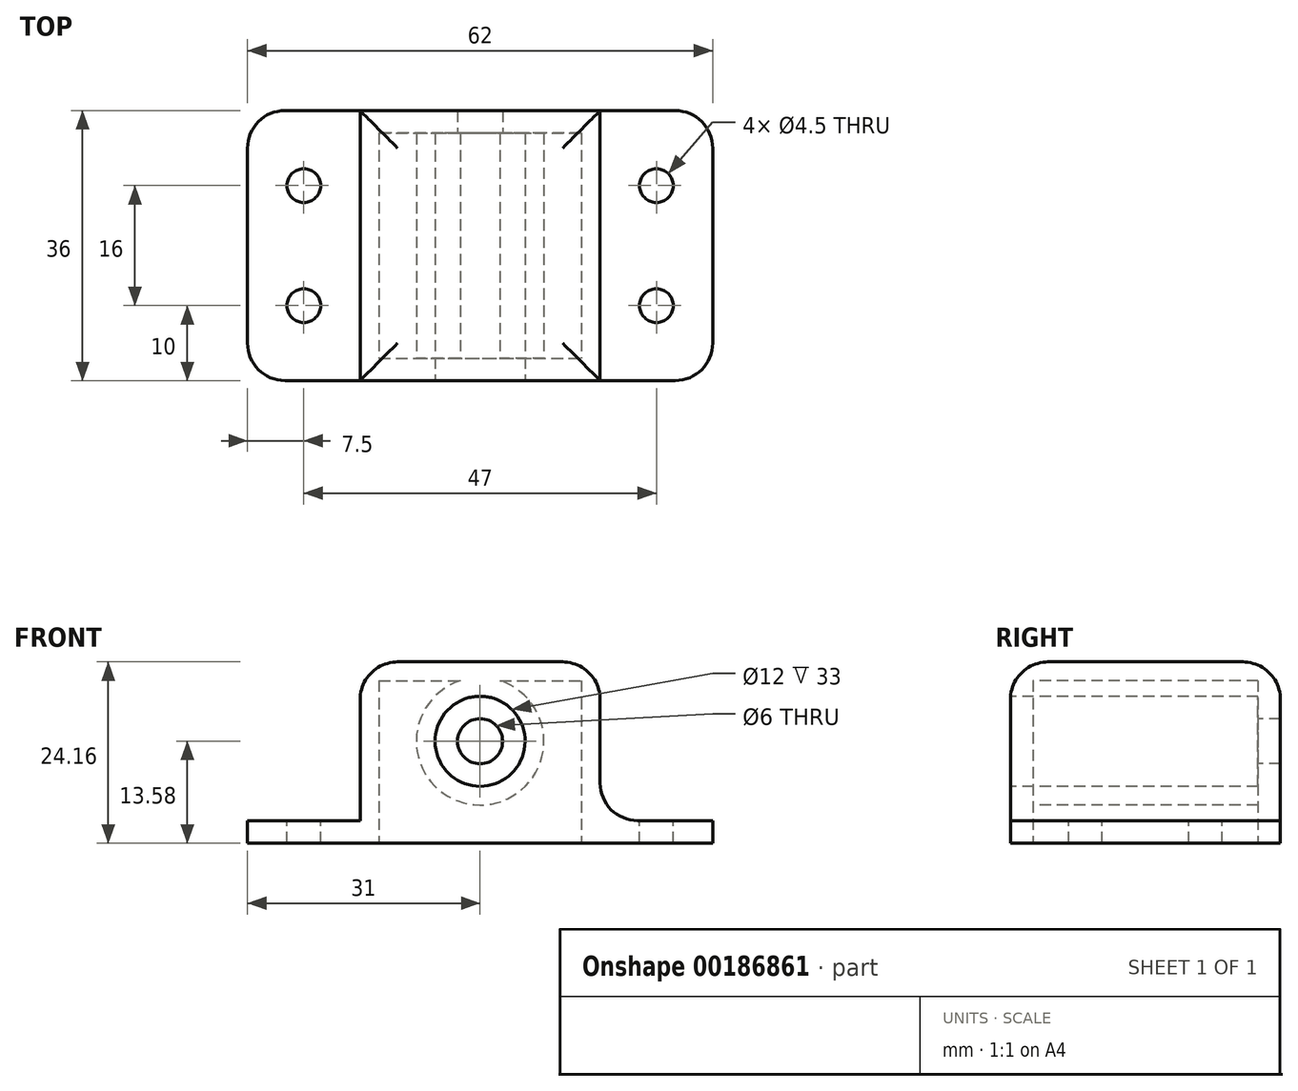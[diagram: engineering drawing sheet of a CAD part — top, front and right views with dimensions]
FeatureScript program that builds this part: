
annotation { "Feature Type Name" : "Feature", "Feature Type Description" : "" }
export const myFeature = defineFeature(function(context is Context, id is Id, definition is map)
    precondition{}
    {
        {
            var Q0;
            Q0=qCreatedBy(makeId("Front.planeOp"),FACE);
            var sketch = newSketch(context, id + "F0", { "sketchPlane" : qUnion([Q0])});
            skPoint(sketch, "E0", {"position": v(0, 0) * mm});
            skCircle(sketch, "E1.MirrorC", {"center": v(0, 0) * mm, "radius": 6 * mm});
            skLineSegment(sketch, "E2.bottom", {"start": v(-16, 10.58) * mm, "end": v(16, 10.58) * mm});
            skLineSegment(sketch, "E2.top", {"start": v(-16, -10.58) * mm, "end": v(16, -10.58) * mm});
            skLineSegment(sketch, "E2.left", {"start": v(-16, 10.58) * mm, "end": v(-16, -10.58) * mm});
            skLineSegment(sketch, "E2.right", {"start": v(16, 10.58) * mm, "end": v(16, -10.58) * mm});
            skSolve(sketch);
        }
        {
            var Q0;
            Q0=qSketchRegion(id+"F0",true);
            var Q1;
            Q1=makeQuery(id+"F0.imprint","IMPRINT",FACE,{"disambiguationData":[TD([[makeQuery(id+"F0.imprint","IMPRINT",EDGE,{"derivedFrom":sQuery(id+"F0.wireOp",EDGE,"yutw9QGI-1s5Z-Afal-mbx2-94IJeUMJpOW0")}),1.0]])]});
            var Q2;
            Q2=makeQuery(id+"F0.imprint","IMPRINT",FACE,{"disambiguationData":[TD([[makeQuery(id+"F0.imprint","IMPRINT",EDGE,{"derivedFrom":sQuery(id+"F0.wireOp",EDGE,"msMzBrXn-RTMr-JK9e-Zdbn-AvcSQ9IQK5gs")}),1.0]])]});
            var Q3;
            Q3=makeQuery(id+"F0.imprint","IMPRINT",FACE,{"disambiguationData":[TD([[makeQuery(id+"F0.imprint","IMPRINT",EDGE,{"derivedFrom":sQuery(id+"F0.wireOp",EDGE,"E1.MirrorC")}),-1.0]])]});
            var Q4;
            Q4=makeQuery(id+"F0.imprint","IMPRINT",FACE,{"disambiguationData":[TD([[makeQuery(id+"F0.imprint","IMPRINT",EDGE,{"derivedFrom":sQuery(id+"F0.wireOp",EDGE,"4545d6f2-485f-4b99-a762-8a09c124ffcd0.MirrorC")}),-1.0]])]});
            extrude(context, id + "F1", {"entities" : qUnion([Q0, Q1, Q2, Q3, Q4]), "oppositeDirection" : true, "depth" : 30 * mm});
        }
        {
            var Q0;
            Q0=makeQuery(id+"F1.opExtrude","CAP_FACE",FACE,{"disambiguationData":[OSD([sQuery(id+"F0.wireOp",EDGE,"E2.bottom"),sQuery(id+"F0.wireOp",EDGE,"E2.top"),sQuery(id+"F0.wireOp",EDGE,"E2.left"),sQuery(id+"F0.wireOp",EDGE,"E2.right")])],"isStart":true});
            var Q1;
            Q1=makeQuery(id+"F1.opExtrude","CAP_FACE",FACE,{"disambiguationData":[OSD([sQuery(id+"F0.wireOp",EDGE,"E2.bottom"),sQuery(id+"F0.wireOp",EDGE,"E2.top"),sQuery(id+"F0.wireOp",EDGE,"E2.left"),sQuery(id+"F0.wireOp",EDGE,"E2.right")])],"isStart":false});
            var Q2;
            Q2=makeQuery(id+"F1.opExtrude","SWEPT_FACE",FACE,{"disambiguationData":[OSD([sQuery(id+"F0.wireOp",EDGE,"E2.top")])]});
            shell(context, id + "F2", {"entities" : qUnion([Q0, Q1, Q2]), "thickness" : 2.5 * mm});
        }
        {
            var Q0;
            Q0=qSketchRegion(id+"F0",true);
            extrude(context, id + "F3", {"entities" : qUnion([Q0]), "operationType" : NewBodyOperationType.ADD, "depth" : 3 * mm});
        }
        {
            var Q0;
            Q0=makeQuery(id+"F1.opExtrude","CAP_FACE",FACE,{"disambiguationData":[OSD([sQuery(id+"F0.wireOp",EDGE,"E2.bottom"),sQuery(id+"F0.wireOp",EDGE,"E2.top"),sQuery(id+"F0.wireOp",EDGE,"E2.left"),sQuery(id+"F0.wireOp",EDGE,"E2.right")])],"isStart":false});
            var sketch = newSketch(context, id + "F4", { "sketchPlane" : qUnion([Q0])});
            skCircle(sketch, "E3.0", {"center": v(0, 0) * mm, "radius": 3 * mm});
            skLineSegment(sketch, "E4.0.0", {"start": v(16, 10.58) * mm, "end": v(-16, 10.58) * mm});
            skLineSegment(sketch, "E4.0.1", {"start": v(-16, 10.58) * mm, "end": v(-16, -10.58) * mm});
            skLineSegment(sketch, "E4.0.2", {"start": v(-16, -10.58) * mm, "end": v(16, -10.58) * mm});
            skLineSegment(sketch, "E4.0.3", {"start": v(16, -10.58) * mm, "end": v(16, 10.58) * mm});
            skSolve(sketch);
        }
        {
            var Q0;
            Q0=qSketchRegion(id+"F4",true);
            extrude(context, id + "F5", {"entities" : qUnion([Q0]), "operationType" : NewBodyOperationType.ADD, "depth" : 3 * mm});
        }
        {
            var Q0;
            Q0=makeQuery(id+"F3.opExtrude","SWEPT_FACE",FACE,{"disambiguationData":[OSD([sQuery(id+"F0.wireOp",EDGE,"E2.top")])]});
            var sketch = newSketch(context, id + "F6", { "sketchPlane" : qUnion([Q0])});
            skLineSegment(sketch, "E5.0.0", {"start": v(-16, 0) * mm, "end": v(16, 0) * mm});
            skLineSegment(sketch, "E5.0.1", {"start": v(16, 0) * mm, "end": v(16, 3) * mm});
            skLineSegment(sketch, "E5.0.2", {"start": v(16, 3) * mm, "end": v(-16, 3) * mm});
            skLineSegment(sketch, "E5.0.3", {"start": v(-16, 3) * mm, "end": v(-16, 0) * mm});
            skLineSegment(sketch, "E6.0.0", {"start": v(13.5, 0) * mm, "end": v(13.5, -30) * mm});
            skLineSegment(sketch, "E6.0.1", {"start": v(13.5, -30) * mm, "end": v(-13.5, -30) * mm});
            skLineSegment(sketch, "E6.0.2", {"start": v(-13.5, -30) * mm, "end": v(-13.5, 0) * mm});
            skLineSegment(sketch, "E6.0.3", {"start": v(-13.5, 0) * mm, "end": v(-16, 0) * mm});
            skLineSegment(sketch, "E6.0.4", {"start": v(-16, 0) * mm, "end": v(-16, -33) * mm});
            skLineSegment(sketch, "E6.0.5", {"start": v(-16, -33) * mm, "end": v(16, -33) * mm});
            skLineSegment(sketch, "E6.0.6", {"start": v(16, -33) * mm, "end": v(16, 0) * mm});
            skLineSegment(sketch, "E6.0.7", {"start": v(16, 0) * mm, "end": v(13.5, 0) * mm});
            skLineSegment(sketch, "E7.bottom", {"start": v(-16, 3) * mm, "end": v(-31, 3) * mm});
            skLineSegment(sketch, "E7.top", {"start": v(-16, -33) * mm, "end": v(-31, -33) * mm});
            skLineSegment(sketch, "E7.left", {"start": v(-16, 3) * mm, "end": v(-16, -33) * mm});
            skLineSegment(sketch, "E7.right", {"start": v(-31, 3) * mm, "end": v(-31, -33) * mm});
            skLineSegment(sketch, "E8", {"start": v(-23.5, 3) * mm, "end": v(-23.5, -33) * mm, "construction": true});
            skLineSegment(sketch, "E9", {"start": v(-31, -15) * mm, "end": v(-16, -15) * mm, "construction": true});
            skCircle(sketch, "E10", {"center": v(-23.5, -7) * mm, "radius": 2.25 * mm});
            skCircle(sketch, "E11.MirrorC", {"center": v(-23.5, -23) * mm, "radius": 2.25 * mm});
            skLineSegment(sketch, "E12.MirrorCS", {"start": v(31, 3) * mm, "end": v(31, -33) * mm});
            skLineSegment(sketch, "E13.MirrorCS", {"start": v(16, 3) * mm, "end": v(31, 3) * mm});
            skLineSegment(sketch, "E14.MirrorCS", {"start": v(16, -33) * mm, "end": v(31, -33) * mm});
            skCircle(sketch, "E15.MirrorC", {"center": v(23.5, -23) * mm, "radius": 2.25 * mm});
            skCircle(sketch, "E16.MirrorC", {"center": v(23.5, -7) * mm, "radius": 2.25 * mm});
            skSolve(sketch);
        }
        {
            var Q0;
            Q0=qSketchRegion(id+"F6",true);
            extrude(context, id + "F7", {"entities" : qUnion([Q0]), "operationType" : NewBodyOperationType.ADD, "depth" : 3 * mm});
        }
        {
            var Q0;
            {var subQ0=sQuery(id+"F0.wireOp",EDGE,"E2.left");var subQ1=sQuery(id+"F0.wireOp",EDGE,"E2.top");Q0=makeQuery(id+"F5.boolean.opBoolean","MERGE",EDGE,{"derivedFrom":[makeQuery(id+"F3.boolean.opBoolean","MERGE",EDGE,{"derivedFrom":[makeQuery(id+"F1.opExtrude","SWEPT_EDGE",EDGE,{"disambiguationData":[OSD([subQ1,subQ0])]}),makeQuery(id+"F3.opExtrude","SWEPT_EDGE",EDGE,{"disambiguationData":[OSD([subQ1,subQ0])]})]}),makeQuery(id+"F5.opExtrude","SWEPT_EDGE",EDGE,{"disambiguationData":[OSD([sQuery(id+"F4.wireOp",EDGE,"E4.0.2"),sQuery(id+"F4.wireOp",EDGE,"E4.0.3")])]})]});}
            var Q1;
            {var subQ0=sQuery(id+"F0.wireOp",EDGE,"E2.right");var subQ1=sQuery(id+"F0.wireOp",EDGE,"E2.top");Q1=makeQuery(id+"F5.boolean.opBoolean","MERGE",EDGE,{"derivedFrom":[makeQuery(id+"F3.boolean.opBoolean","MERGE",EDGE,{"derivedFrom":[makeQuery(id+"F1.opExtrude","SWEPT_EDGE",EDGE,{"disambiguationData":[OSD([subQ1,subQ0])]}),makeQuery(id+"F3.opExtrude","SWEPT_EDGE",EDGE,{"disambiguationData":[OSD([subQ1,subQ0])]})]}),makeQuery(id+"F5.opExtrude","SWEPT_EDGE",EDGE,{"disambiguationData":[OSD([sQuery(id+"F4.wireOp",EDGE,"E4.0.1"),sQuery(id+"F4.wireOp",EDGE,"E4.0.2")])]})]});}
            var Q2;
            {var subQ0=sQuery(id+"F0.wireOp",EDGE,"E2.left");var subQ1=sQuery(id+"F0.wireOp",EDGE,"E2.bottom");Q2=makeQuery(id+"F5.boolean.opBoolean","MERGE",EDGE,{"derivedFrom":[makeQuery(id+"F3.boolean.opBoolean","MERGE",EDGE,{"derivedFrom":[makeQuery(id+"F1.opExtrude","SWEPT_EDGE",EDGE,{"disambiguationData":[OSD([subQ1,subQ0])]}),makeQuery(id+"F3.opExtrude","SWEPT_EDGE",EDGE,{"disambiguationData":[OSD([subQ1,subQ0])]})]}),makeQuery(id+"F5.opExtrude","SWEPT_EDGE",EDGE,{"disambiguationData":[OSD([sQuery(id+"F4.wireOp",EDGE,"E4.0.0"),sQuery(id+"F4.wireOp",EDGE,"E4.0.3")])]})]});}
            var Q3;
            {var subQ0=sQuery(id+"F0.wireOp",EDGE,"E2.right");var subQ1=sQuery(id+"F0.wireOp",EDGE,"E2.bottom");Q3=makeQuery(id+"F5.boolean.opBoolean","MERGE",EDGE,{"derivedFrom":[makeQuery(id+"F3.boolean.opBoolean","MERGE",EDGE,{"derivedFrom":[makeQuery(id+"F1.opExtrude","SWEPT_EDGE",EDGE,{"disambiguationData":[OSD([subQ1,subQ0])]}),makeQuery(id+"F3.opExtrude","SWEPT_EDGE",EDGE,{"disambiguationData":[OSD([subQ1,subQ0])]})]}),makeQuery(id+"F5.opExtrude","SWEPT_EDGE",EDGE,{"disambiguationData":[OSD([sQuery(id+"F4.wireOp",EDGE,"E4.0.0"),sQuery(id+"F4.wireOp",EDGE,"E4.0.1")])]})]});}
            var Q4;
            Q4=makeQuery(id+"F3.opExtrude","CAP_EDGE",EDGE,{"disambiguationData":[OSD([sQuery(id+"F0.wireOp",EDGE,"E2.bottom")])],"isStart":false});
            var Q5;
            Q5=makeQuery(id+"F5.opExtrude","CAP_EDGE",EDGE,{"disambiguationData":[OSD([sQuery(id+"F4.wireOp",EDGE,"E4.0.0")])],"isStart":false});
            var Q6;
            Q6=makeQuery(id+"F7.opExtrude","SWEPT_EDGE",EDGE,{"disambiguationData":[OSD([sQuery(id+"F6.wireOp",EDGE,"E12.MirrorCS"),sQuery(id+"F6.wireOp",EDGE,"E13.MirrorCS")])]});
            var Q7;
            Q7=makeQuery(id+"F7.opExtrude","SWEPT_EDGE",EDGE,{"disambiguationData":[OSD([sQuery(id+"F6.wireOp",EDGE,"E12.MirrorCS"),sQuery(id+"F6.wireOp",EDGE,"E14.MirrorCS")])]});
            var Q8;
            Q8=makeQuery(id+"F7.opExtrude","SWEPT_EDGE",EDGE,{"disambiguationData":[OSD([sQuery(id+"F6.wireOp",EDGE,"E7.bottom"),sQuery(id+"F6.wireOp",EDGE,"E7.right")])]});
            var Q9;
            Q9=makeQuery(id+"F7.opExtrude","SWEPT_EDGE",EDGE,{"disambiguationData":[OSD([sQuery(id+"F6.wireOp",EDGE,"E7.top"),sQuery(id+"F6.wireOp",EDGE,"E7.right")])]});
            fillet(context, id + "F8", {"entities" : qUnion([Q0, Q1, Q2, Q3, Q4, Q5, Q6, Q7, Q8, Q9]), "radius" : 5 * mm, "tangentPropagation" : true, "allowEdgeOverflow" : false});
        }
    });
